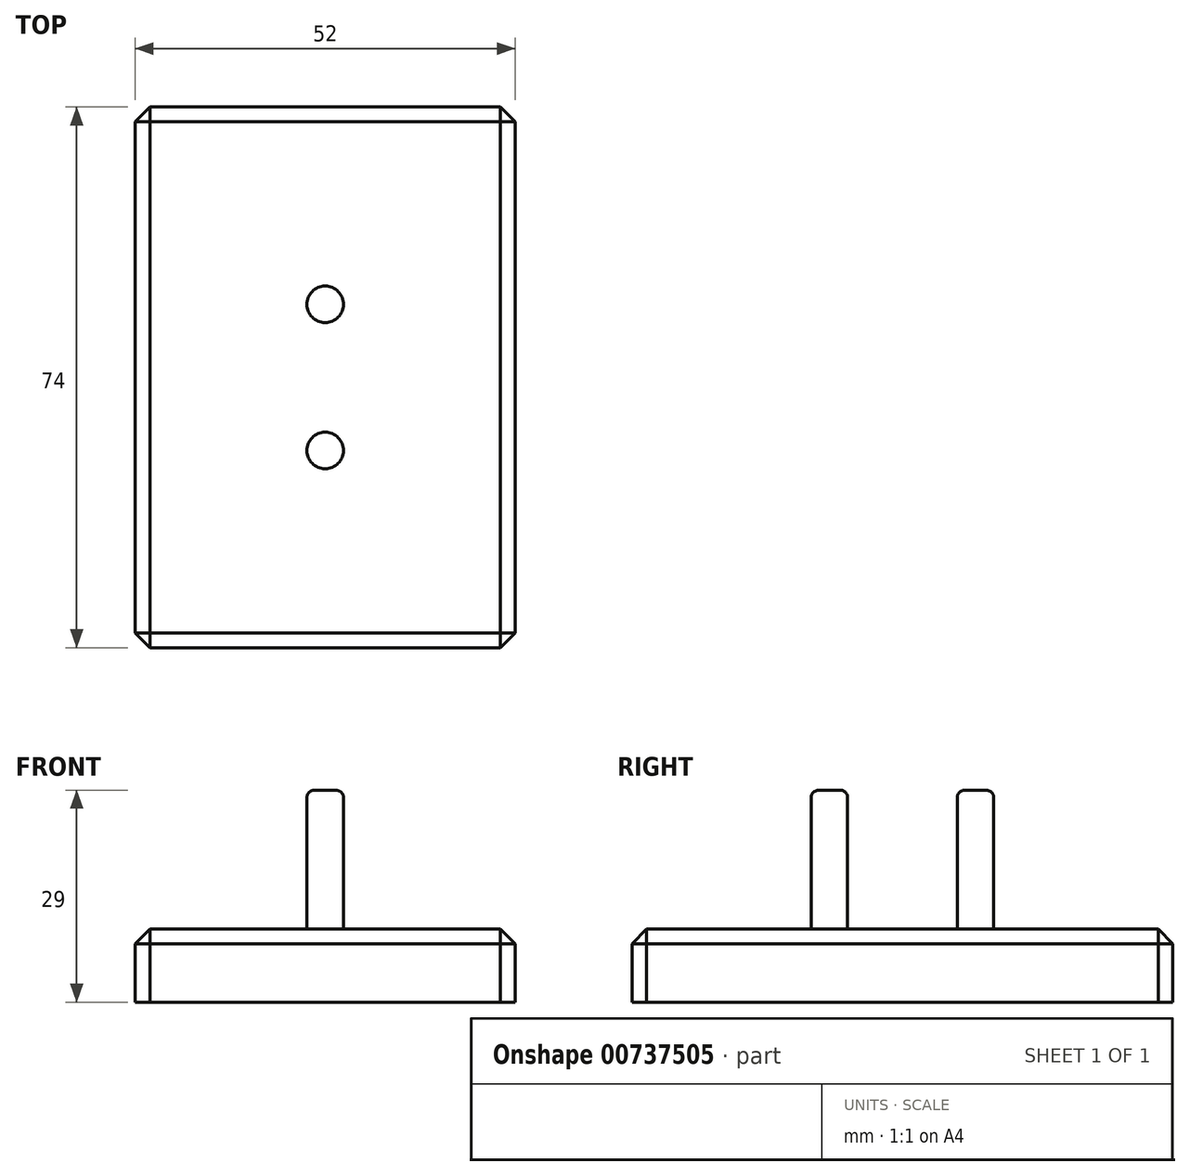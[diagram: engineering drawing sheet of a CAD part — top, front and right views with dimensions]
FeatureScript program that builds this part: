
annotation { "Feature Type Name" : "Feature", "Feature Type Description" : "" }
export const myFeature = defineFeature(function(context is Context, id is Id, definition is map)
    precondition{}
    {
        {
            var Q0;
            Q0=qCreatedBy(makeId("Top.planeOp"),FACE);
            var sketch = newSketch(context, id + "F0", { "sketchPlane" : qUnion([Q0])});
            skLineSegment(sketch, "E0.bottom", {"start": v(26, 37) * mm, "end": v(26, -37) * mm});
            skLineSegment(sketch, "E0.top", {"start": v(-26, 37) * mm, "end": v(-26, -37) * mm});
            skLineSegment(sketch, "E0.left", {"start": v(26, 37) * mm, "end": v(-26, 37) * mm});
            skLineSegment(sketch, "E0.right", {"start": v(26, -37) * mm, "end": v(-26, -37) * mm});
            skLineSegment(sketch, "E1", {"start": v(-26, 37) * mm, "end": v(26, -37) * mm, "construction": true});
            skLineSegment(sketch, "E2", {"start": v(26, 37) * mm, "end": v(-26, -37) * mm, "construction": true});
            skSolve(sketch);
        }
        {
            var Q0;
            Q0=makeQuery(id+"F0.imprint","IMPRINT",FACE,{"disambiguationData":[TD([[makeQuery(id+"F0.imprint","IMPRINT",EDGE,{"derivedFrom":sQuery(id+"F0.wireOp",EDGE,"E0.bottom")}),-1.0]])]});
            extrude(context, id + "F1", {"entities" : qUnion([Q0]), "depth" : 10 * mm, "offsetDistance" : 25 * mm});
        }
        {
            var Q0;
            Q0=makeQuery(id+"F1.opExtrude","CAP_FACE",FACE,{"disambiguationData":[OSD([sQuery(id+"F0.wireOp",EDGE,"E0.bottom"),sQuery(id+"F0.wireOp",EDGE,"E0.top"),sQuery(id+"F0.wireOp",EDGE,"E0.left"),sQuery(id+"F0.wireOp",EDGE,"E0.right")])],"isStart":false});
            var sketch = newSketch(context, id + "F2", { "sketchPlane" : qUnion([Q0])});
            skCircle(sketch, "E3", {"center": v(0, 10) * mm, "radius": 2.5 * mm});
            skCircle(sketch, "E4", {"center": v(0, -10) * mm, "radius": 2.5 * mm});
            skSolve(sketch);
        }
        {
            var Q0;
            Q0 = qSketchRegion(id + "F2", true);
            extrude(context, id + "F3", {"entities" : qUnion([Q0]), "operationType" : NewBodyOperationType.ADD, "depth" : 19 * mm, "offsetDistance" : 25 * mm});
        }
        {
            var Q0;
            Q0=makeQuery(id+"F3.opExtrude","CAP_EDGE",EDGE,{"disambiguationData":[OSD([sQuery(id+"F2.wireOp",EDGE,"E3")])],"isStart":false});
            var Q1;
            Q1=makeQuery(id+"F3.opExtrude","CAP_EDGE",EDGE,{"disambiguationData":[OSD([sQuery(id+"F2.wireOp",EDGE,"E4")])],"isStart":false});
            fillet(context, id + "F4", {"entities" : qUnion([Q0, Q1]), "radius" : 1 * mm, "tangentPropagation" : true, "allowEdgeOverflow" : false});
        }
        {
            var Q0;
            Q0=makeQuery(id+"F1.opExtrude","CAP_EDGE",EDGE,{"disambiguationData":[OSD([sQuery(id+"F0.wireOp",EDGE,"E0.left")])],"isStart":false});
            var Q1;
            Q1=makeQuery(id+"F1.opExtrude","CAP_EDGE",EDGE,{"disambiguationData":[OSD([sQuery(id+"F0.wireOp",EDGE,"E0.bottom")])],"isStart":false});
            var Q2;
            Q2=makeQuery(id+"F1.opExtrude","CAP_EDGE",EDGE,{"disambiguationData":[OSD([sQuery(id+"F0.wireOp",EDGE,"E0.top")])],"isStart":false});
            var Q3;
            Q3=makeQuery(id+"F1.opExtrude","CAP_EDGE",EDGE,{"disambiguationData":[OSD([sQuery(id+"F0.wireOp",EDGE,"E0.right")])],"isStart":false});
            var Q4;
            Q4=makeQuery(id+"F1.opExtrude","SWEPT_EDGE",EDGE,{"disambiguationData":[OSD([sQuery(id+"F0.wireOp",EDGE,"E0.top"),sQuery(id+"F0.wireOp",EDGE,"E0.right")])]});
            var Q5;
            Q5=makeQuery(id+"F1.opExtrude","SWEPT_EDGE",EDGE,{"disambiguationData":[OSD([sQuery(id+"F0.wireOp",EDGE,"E0.bottom"),sQuery(id+"F0.wireOp",EDGE,"E0.right")])]});
            var Q6;
            Q6=makeQuery(id+"F1.opExtrude","SWEPT_EDGE",EDGE,{"disambiguationData":[OSD([sQuery(id+"F0.wireOp",EDGE,"E0.top"),sQuery(id+"F0.wireOp",EDGE,"E0.left")])]});
            var Q7;
            Q7=makeQuery(id+"F1.opExtrude","SWEPT_EDGE",EDGE,{"disambiguationData":[OSD([sQuery(id+"F0.wireOp",EDGE,"E0.bottom"),sQuery(id+"F0.wireOp",EDGE,"E0.left")])]});
            chamfer(context, id + "F5", {"entities" : qUnion([Q0, Q1, Q2, Q3, Q4, Q5, Q6, Q7]), "width" : 2 * mm, "tangentPropagation" : true});
        }
    });
